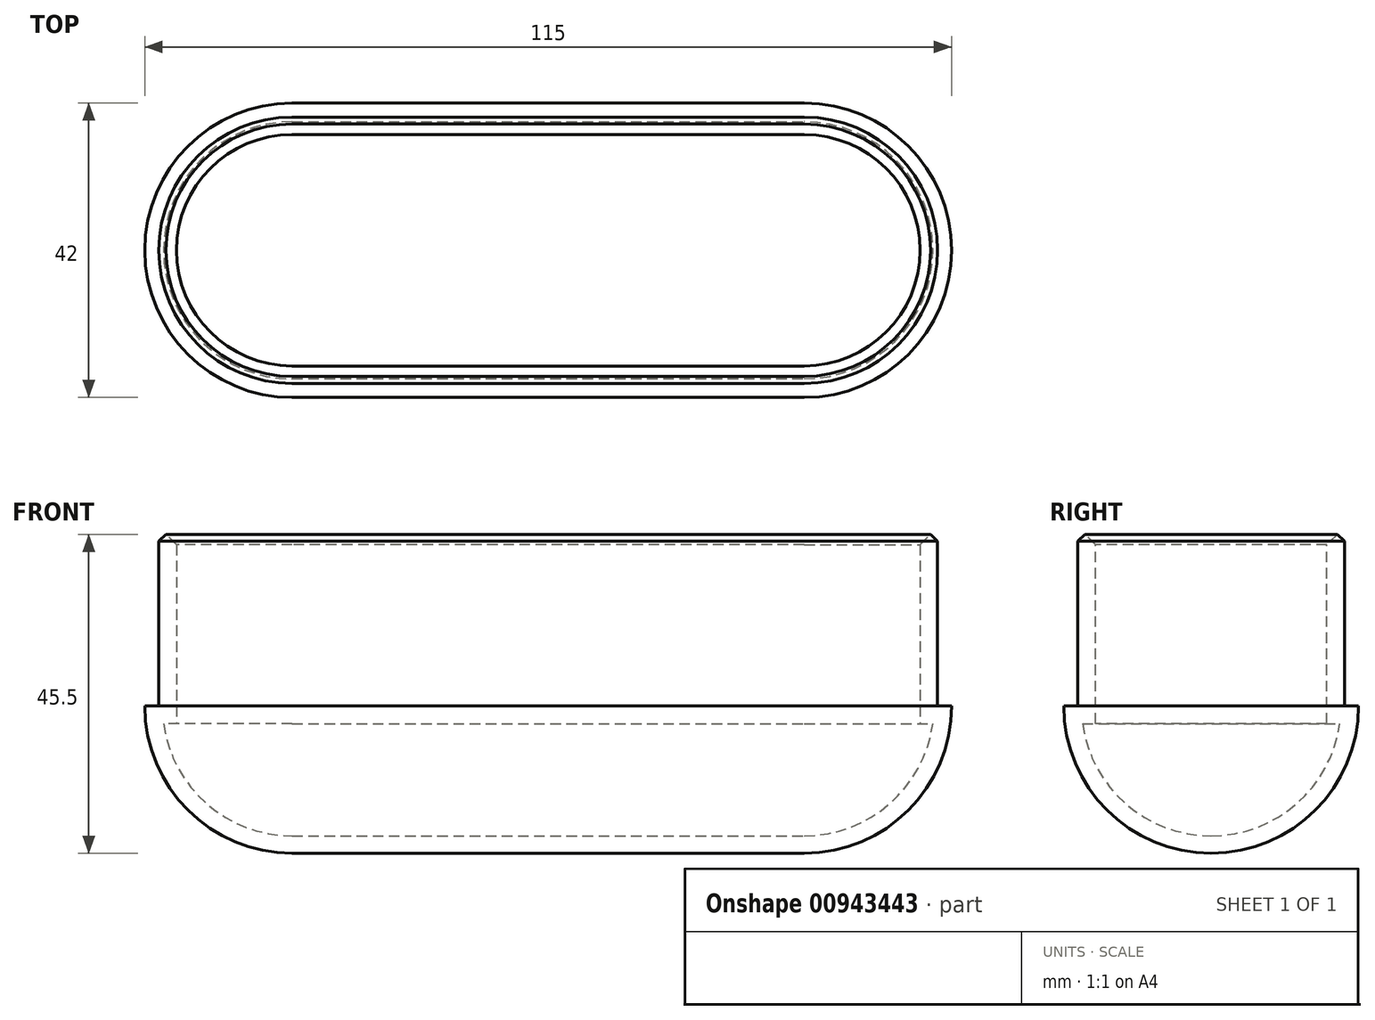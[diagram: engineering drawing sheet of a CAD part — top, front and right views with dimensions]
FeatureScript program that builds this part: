
annotation { "Feature Type Name" : "Feature", "Feature Type Description" : "" }
export const myFeature = defineFeature(function(context is Context, id is Id, definition is map)
    precondition{}
    {
        {
            var Q0;
            Q0=qCreatedBy(makeId("Top.planeOp"),FACE);
            var sketch = newSketch(context, id + "F0", { "sketchPlane" : qUnion([Q0])});
            skLineSegment(sketch, "E0.bottom", {"start": v(-36.5, 21) * mm, "end": v(36.5, 21) * mm});
            skLineSegment(sketch, "E0.top", {"start": v(-36.5, -21) * mm, "end": v(36.5, -21) * mm});
            skLineSegment(sketch, "E0.left", {"start": v(-57.5, 0) * mm, "end": v(-57.5, 0) * mm});
            skLineSegment(sketch, "E0.right", {"start": v(57.5, 0) * mm, "end": v(57.5, 0) * mm});
            skPoint(sketch, "E0.middle", {"position": v(0, 0) * mm});
            skLineSegment(sketch, "E1.bottom", {"start": v(-36.5, -19) * mm, "end": v(36.5, -19) * mm});
            skLineSegment(sketch, "E1.top", {"start": v(-36.5, 19) * mm, "end": v(36.5, 19) * mm});
            skLineSegment(sketch, "E1.left", {"start": v(-55.5, 0) * mm, "end": v(-55.5, 0) * mm});
            skLineSegment(sketch, "E1.right", {"start": v(55.5, 0) * mm, "end": v(55.5, 0) * mm});
            skPoint(sketch, "E2.visualSharp", {"position": v(-57.5, 21) * mm});
            skArc(sketch, "E2.filletArc", {"start": v(-36.5, 21) * mm, "mid": v(-51.35, 14.85) * mm, "end": v(-57.5, 0) * mm});
            skPoint(sketch, "E3.visualSharp", {"position": v(-57.5, -21) * mm});
            skArc(sketch, "E3.filletArc", {"start": v(-57.5, 0) * mm, "mid": v(-51.35, -14.85) * mm, "end": v(-36.5, -21) * mm});
            skPoint(sketch, "E4.visualSharp", {"position": v(57.5, -21) * mm});
            skArc(sketch, "E4.filletArc", {"start": v(36.5, -21) * mm, "mid": v(51.35, -14.85) * mm, "end": v(57.5, 0) * mm});
            skPoint(sketch, "E5.visualSharp", {"position": v(57.5, 21) * mm});
            skArc(sketch, "E5.filletArc", {"start": v(57.5, 0) * mm, "mid": v(51.35, 14.85) * mm, "end": v(36.5, 21) * mm});
            skPoint(sketch, "E6.visualSharp", {"position": v(-55.5, 19) * mm});
            skArc(sketch, "E6.filletArc", {"start": v(-36.5, 19) * mm, "mid": v(-49.94, 13.44) * mm, "end": v(-55.5, 0) * mm});
            skPoint(sketch, "E7.visualSharp", {"position": v(-55.5, -19) * mm});
            skArc(sketch, "E7.filletArc", {"start": v(-55.5, 0) * mm, "mid": v(-49.94, -13.44) * mm, "end": v(-36.5, -19) * mm});
            skPoint(sketch, "E8.visualSharp", {"position": v(55.5, -19) * mm});
            skArc(sketch, "E8.filletArc", {"start": v(36.5, -19) * mm, "mid": v(49.94, -13.44) * mm, "end": v(55.5, 0) * mm});
            skPoint(sketch, "E9.visualSharp", {"position": v(55.5, 19) * mm});
            skArc(sketch, "E9.filletArc", {"start": v(55.5, 0) * mm, "mid": v(49.94, 13.44) * mm, "end": v(36.5, 19) * mm});
            skSolve(sketch);
        }
        {
            var Q0;
            Q0=makeQuery(id+"F0.imprint","IMPRINT",FACE,{"disambiguationData":[TD([[makeQuery(id+"F0.imprint","IMPRINT",EDGE,{"derivedFrom":sQuery(id+"F0.wireOp",EDGE,"E1.bottom")}),1.0]])]});
            extrude(context, id + "F1", {"entities" : qUnion([Q0]), "depth" : 25 * mm, "offsetDistance" : 25 * mm});
        }
        {
            var Q0;
            Q0=makeQuery(id+"F0.imprint","IMPRINT",FACE,{"disambiguationData":[TD([[makeQuery(id+"F0.imprint","IMPRINT",EDGE,{"derivedFrom":sQuery(id+"F0.wireOp",EDGE,"E0.bottom")}),-1.0]])]});
            var Q1;
            Q1=makeQuery(id+"F0.imprint","IMPRINT",FACE,{"disambiguationData":[TD([[makeQuery(id+"F0.imprint","IMPRINT",EDGE,{"derivedFrom":sQuery(id+"F0.wireOp",EDGE,"E1.bottom")}),1.0]])]});
            extrude(context, id + "F2", {"entities" : qUnion([Q0, Q1]), "operationType" : NewBodyOperationType.ADD, "oppositeDirection" : true, "depth" : 21 * mm, "offsetDistance" : 25 * mm});
        }
        {
            var Q0;
            Q0=makeQuery(id+"F2.opExtrude","CAP_EDGE",EDGE,{"disambiguationData":[OSD([sQuery(id+"F0.wireOp",EDGE,"E0.bottom")])],"isStart":false});
            fillet(context, id + "F3", {"entities" : qUnion([Q0]), "radius" : 21 * mm, "tangentPropagation" : true, "allowEdgeOverflow" : false});
        }
        {
            var Q0;
            Q0=makeQuery(id+"F1.opExtrude","CAP_FACE",FACE,{"disambiguationData":[OSD([sQuery(id+"F0.wireOp",EDGE,"E1.bottom"),sQuery(id+"F0.wireOp",EDGE,"E1.top"),sQuery(id+"F0.wireOp",EDGE,"E6.filletArc"),sQuery(id+"F0.wireOp",EDGE,"E7.filletArc"),sQuery(id+"F0.wireOp",EDGE,"E8.filletArc"),sQuery(id+"F0.wireOp",EDGE,"E9.filletArc")])],"isStart":false});
            shell(context, id + "F4", {"entities" : qUnion([Q0]), "thickness" : 2.5 * mm});
        }
        {
            var Q0;
            Q0=makeQuery(id+"F1.opExtrude","CAP_EDGE",EDGE,{"disambiguationData":[OSD([sQuery(id+"F0.wireOp",EDGE,"E1.top")])],"isStart":false});
            chamfer(context, id + "F5", {"entities" : qUnion([Q0]), "width" : 1.5 * mm, "tangentPropagation" : true});
        }
        {
            var Q0;
            {var subQ0=sQuery(id+"F0.wireOp",EDGE,"E1.bottom");Q0=makeQuery(id+"F4.opShell","OFFSET_EDGE",EDGE,{"disambiguationData":[OSD([subQ0]),TDD([makeQuery(id+"F1.opExtrude","CAP_EDGE",EDGE,{"disambiguationData":[OSD([subQ0])],"isStart":true})])]});}
            chamfer(context, id + "F6", {"entities" : qUnion([Q0]), "width" : 2 * mm, "tangentPropagation" : true});
        }
    });
